# Revit family: 13157CHN_new
name_source: partatom
category: Plumbing Fixtures
units: mm (PartAtom-declared; Revit-internal decimal feet)

## family parameters
Always vertical = No
Cut with Voids When Loaded = No
OmniClass Number = 23.31.11.00
OmniClass Title = Faucets
Part Type = Normal
Room Calculation Point = No
Round Connector Dimension = Use Diameter
Shared = No
Work Plane-Based = Yes

## types (1)
- 007 Chrome
    Connector Description = Water Inlet 12.7mm
    Default Elevation = 1219 mm
    Description = ShowerTablet Select Bath thermostat 360 for exposed installation
    Diameter = 13 mm
    Manufacturer = Hansgrohe
    Material = Hansgrohe - Metal - 007 Chrome
    Model = 13157CHN
    Product Guid = 782656b6-845e-426b-9c0c-c468ed3585f5
    Product Page URL = https://www.hansgrohe.com
    Product data url = https://bimobject.com
    URL = https://www.hansgrohe.com
    Version = 1

## geometry (parser evidence)
native form markers: Sweep x3
no freeform markers — native parametric forms only
